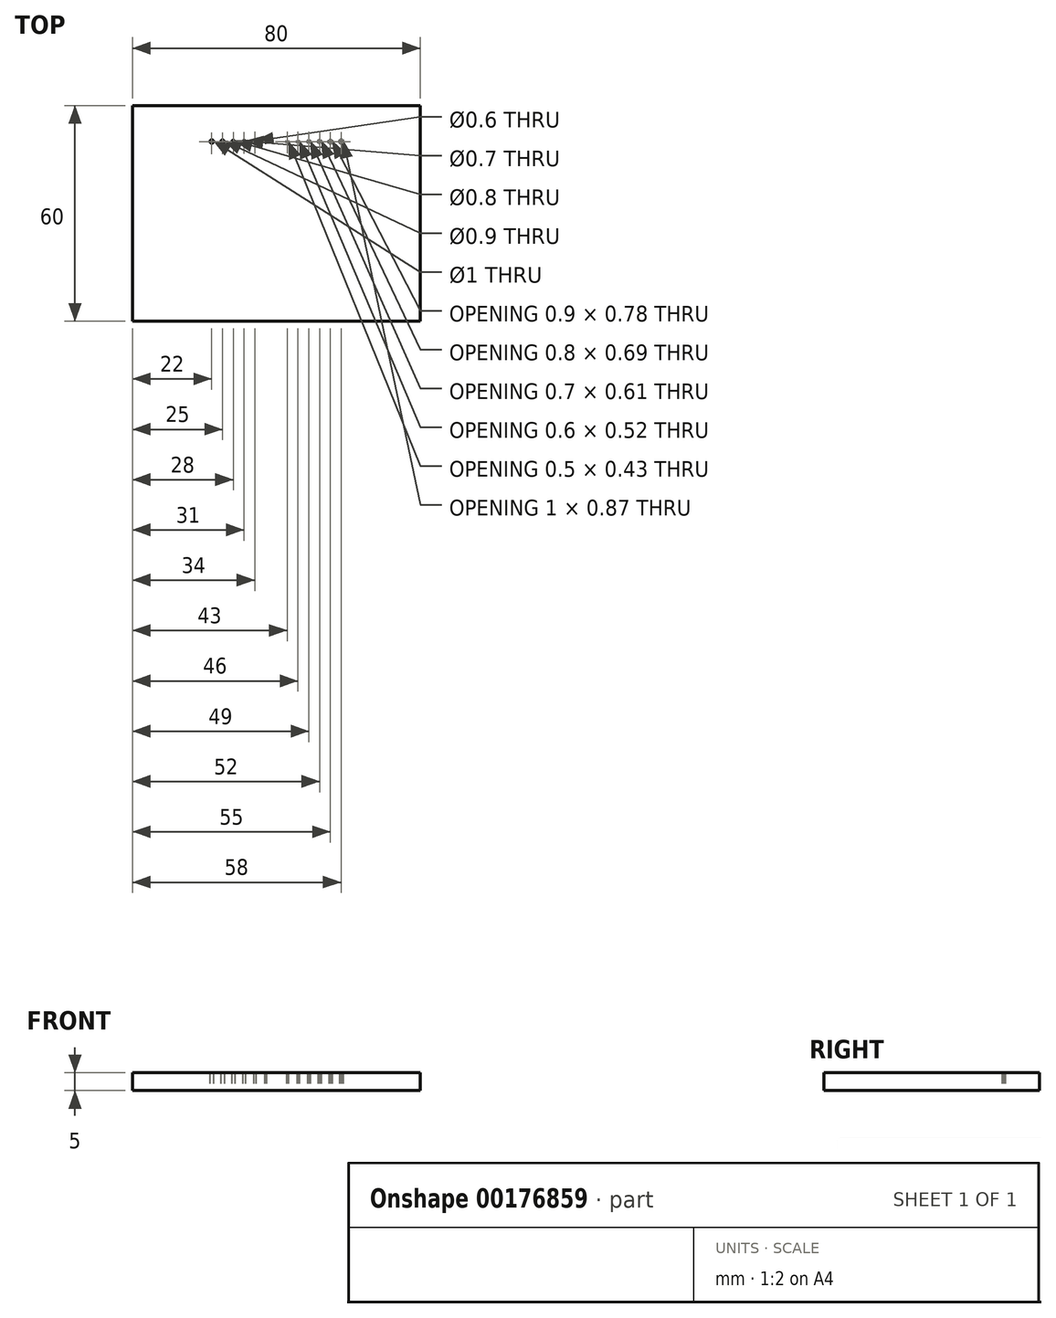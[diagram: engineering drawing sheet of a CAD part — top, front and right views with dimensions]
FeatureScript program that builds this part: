
annotation { "Feature Type Name" : "Feature", "Feature Type Description" : "" }
export const myFeature = defineFeature(function(context is Context, id is Id, definition is map)
    precondition{}
    {
        {
            var Q0;
            Q0=qCreatedBy(makeId("Top.planeOp"),FACE);
            var sketch = newSketch(context, id + "F0", { "sketchPlane" : qUnion([Q0])});
            skLineSegment(sketch, "E0.bottom", {"start": v(40, 30) * mm, "end": v(-40, 30) * mm});
            skLineSegment(sketch, "E0.top", {"start": v(40, -30) * mm, "end": v(-40, -30) * mm});
            skLineSegment(sketch, "E0.left", {"start": v(40, 30) * mm, "end": v(40, -30) * mm});
            skLineSegment(sketch, "E0.right", {"start": v(-40, 30) * mm, "end": v(-40, -30) * mm});
            skPoint(sketch, "E0.middle", {"position": v(0, 0) * mm});
            skLineSegment(sketch, "E1", {"start": v(-54.66, 20) * mm, "end": v(60.66, 20) * mm, "construction": true});
            skCircle(sketch, "E2", {"center": v(-18, 20) * mm, "radius": 0.5 * mm});
            skCircle(sketch, "E3", {"center": v(-15, 20) * mm, "radius": 0.45 * mm});
            skCircle(sketch, "E4", {"center": v(-12, 20) * mm, "radius": 0.4 * mm});
            skCircle(sketch, "E5", {"center": v(-9, 20) * mm, "radius": 0.35 * mm});
            skCircle(sketch, "E6", {"center": v(-6, 20) * mm, "radius": 0.3 * mm});
            skCircle(sketch, "E7", {"center": v(-3, 20) * mm, "radius": 0.25 * mm});
            skCircle(sketch, "E8.cCircle", {"center": v(18, 20) * mm, "radius": 0.43 * mm, "construction": true});
            skLineSegment(sketch, "E8.0", {"start": v(18.25, 19.57) * mm, "end": v(17.75, 19.57) * mm});
            skLineSegment(sketch, "E8.1", {"start": v(17.75, 19.57) * mm, "end": v(17.5, 20) * mm});
            skLineSegment(sketch, "E8.2", {"start": v(17.5, 20) * mm, "end": v(17.75, 20.43) * mm});
            skLineSegment(sketch, "E8.3", {"start": v(17.75, 20.43) * mm, "end": v(18.25, 20.43) * mm});
            skLineSegment(sketch, "E8.4", {"start": v(18.25, 20.43) * mm, "end": v(18.5, 20) * mm});
            skLineSegment(sketch, "E8.5", {"start": v(18.5, 20) * mm, "end": v(18.25, 19.57) * mm});
            skPoint(sketch, "E8.0.midPoint", {"position": v(18, 19.57) * mm});
            skCircle(sketch, "E9.cCircle", {"center": v(3, 20) * mm, "radius": 0.22 * mm, "construction": true});
            skLineSegment(sketch, "E9.0", {"start": v(3.13, 20.22) * mm, "end": v(3.25, 20) * mm});
            skLineSegment(sketch, "E9.1", {"start": v(3.25, 20) * mm, "end": v(3.12, 19.78) * mm});
            skLineSegment(sketch, "E9.2", {"start": v(3.12, 19.78) * mm, "end": v(2.87, 19.78) * mm});
            skLineSegment(sketch, "E9.3", {"start": v(2.87, 19.78) * mm, "end": v(2.75, 20) * mm});
            skLineSegment(sketch, "E9.4", {"start": v(2.75, 20) * mm, "end": v(2.88, 20.22) * mm});
            skLineSegment(sketch, "E9.5", {"start": v(2.88, 20.22) * mm, "end": v(3.13, 20.22) * mm});
            skPoint(sketch, "E9.0.midPoint", {"position": v(3.19, 20.1) * mm});
            skCircle(sketch, "E10.cCircle", {"center": v(6, 20) * mm, "radius": 0.26 * mm, "construction": true});
            skLineSegment(sketch, "E10.0", {"start": v(6.15, 20.26) * mm, "end": v(6.3, 20) * mm});
            skLineSegment(sketch, "E10.1", {"start": v(6.3, 20) * mm, "end": v(6.15, 19.74) * mm});
            skLineSegment(sketch, "E10.2", {"start": v(6.15, 19.74) * mm, "end": v(5.85, 19.74) * mm});
            skLineSegment(sketch, "E10.3", {"start": v(5.85, 19.74) * mm, "end": v(5.7, 20) * mm});
            skLineSegment(sketch, "E10.4", {"start": v(5.7, 20) * mm, "end": v(5.85, 20.26) * mm});
            skLineSegment(sketch, "E10.5", {"start": v(5.85, 20.26) * mm, "end": v(6.15, 20.26) * mm});
            skPoint(sketch, "E10.0.midPoint", {"position": v(6.22, 20.13) * mm});
            skCircle(sketch, "E11.cCircle", {"center": v(9, 20) * mm, "radius": 0.3 * mm, "construction": true});
            skLineSegment(sketch, "E11.0", {"start": v(9.17, 20.3) * mm, "end": v(9.35, 20) * mm});
            skLineSegment(sketch, "E11.1", {"start": v(9.35, 20) * mm, "end": v(9.17, 19.7) * mm});
            skLineSegment(sketch, "E11.2", {"start": v(9.17, 19.7) * mm, "end": v(8.83, 19.7) * mm});
            skLineSegment(sketch, "E11.3", {"start": v(8.83, 19.7) * mm, "end": v(8.65, 20) * mm});
            skLineSegment(sketch, "E11.4", {"start": v(8.65, 20) * mm, "end": v(8.83, 20.3) * mm});
            skLineSegment(sketch, "E11.5", {"start": v(8.83, 20.3) * mm, "end": v(9.17, 20.3) * mm});
            skPoint(sketch, "E11.0.midPoint", {"position": v(9.26, 20.15) * mm});
            skCircle(sketch, "E12.cCircle", {"center": v(12, 20) * mm, "radius": 0.35 * mm, "construction": true});
            skLineSegment(sketch, "E12.0", {"start": v(12.2, 20.35) * mm, "end": v(12.4, 20) * mm});
            skLineSegment(sketch, "E12.1", {"start": v(12.4, 20) * mm, "end": v(12.2, 19.65) * mm});
            skLineSegment(sketch, "E12.2", {"start": v(12.2, 19.65) * mm, "end": v(11.8, 19.65) * mm});
            skLineSegment(sketch, "E12.3", {"start": v(11.8, 19.65) * mm, "end": v(11.6, 20) * mm});
            skLineSegment(sketch, "E12.4", {"start": v(11.6, 20) * mm, "end": v(11.8, 20.35) * mm});
            skLineSegment(sketch, "E12.5", {"start": v(11.8, 20.35) * mm, "end": v(12.2, 20.35) * mm});
            skPoint(sketch, "E12.0.midPoint", {"position": v(12.3, 20.17) * mm});
            skCircle(sketch, "E13.cCircle", {"center": v(15, 20) * mm, "radius": 0.39 * mm, "construction": true});
            skLineSegment(sketch, "E13.0", {"start": v(15.22, 20.39) * mm, "end": v(15.45, 20) * mm});
            skLineSegment(sketch, "E13.1", {"start": v(15.45, 20) * mm, "end": v(15.22, 19.61) * mm});
            skLineSegment(sketch, "E13.2", {"start": v(15.22, 19.61) * mm, "end": v(14.77, 19.61) * mm});
            skLineSegment(sketch, "E13.3", {"start": v(14.78, 19.61) * mm, "end": v(14.55, 20) * mm});
            skLineSegment(sketch, "E13.4", {"start": v(14.55, 20) * mm, "end": v(14.78, 20.39) * mm});
            skLineSegment(sketch, "E13.5", {"start": v(14.77, 20.39) * mm, "end": v(15.22, 20.39) * mm});
            skPoint(sketch, "E13.0.midPoint", {"position": v(15.34, 20.2) * mm});
            skLineSegment(sketch, "E14", {"start": v(3, 44.2) * mm, "end": v(3, -34.47) * mm, "construction": true});
            skLineSegment(sketch, "E15", {"start": v(6, -34.47) * mm, "end": v(6, 45.04) * mm, "construction": true});
            skLineSegment(sketch, "E16", {"start": v(9, 45.04) * mm, "end": v(9, -34.47) * mm, "construction": true});
            skLineSegment(sketch, "E17", {"start": v(12, -34.47) * mm, "end": v(12, 45.04) * mm, "construction": true});
            skLineSegment(sketch, "E18", {"start": v(15, 45.04) * mm, "end": v(15, -34.47) * mm, "construction": true});
            skLineSegment(sketch, "E19", {"start": v(18, -34.47) * mm, "end": v(18, 45.04) * mm, "construction": true});
            skLineSegment(sketch, "E20", {"start": v(-3, 43.62) * mm, "end": v(-3, -34.65) * mm, "construction": true});
            skLineSegment(sketch, "E21", {"start": v(-6, -34.65) * mm, "end": v(-6, 44.07) * mm, "construction": true});
            skLineSegment(sketch, "E22", {"start": v(-9, 44.07) * mm, "end": v(-9, -34.65) * mm, "construction": true});
            skLineSegment(sketch, "E23", {"start": v(-12, -35.1) * mm, "end": v(-12, 45.11) * mm, "construction": true});
            skLineSegment(sketch, "E24", {"start": v(-15, 44.96) * mm, "end": v(-15, -35.1) * mm, "construction": true});
            skLineSegment(sketch, "E25", {"start": v(-18, -35.1) * mm, "end": v(-18, 44.81) * mm, "construction": true});
            skSolve(sketch);
        }
        {
            var Q0;
            Q0=makeQuery(id+"F0.imprint","IMPRINT",FACE,{"disambiguationData":[TD([[makeQuery(id+"F0.imprint","IMPRINT",EDGE,{"derivedFrom":sQuery(id+"F0.wireOp",EDGE,"E0.bottom")}),1.0]])]});
            extrude(context, id + "F1", {"entities" : qUnion([Q0]), "depth" : 5 * mm});
        }
    });
